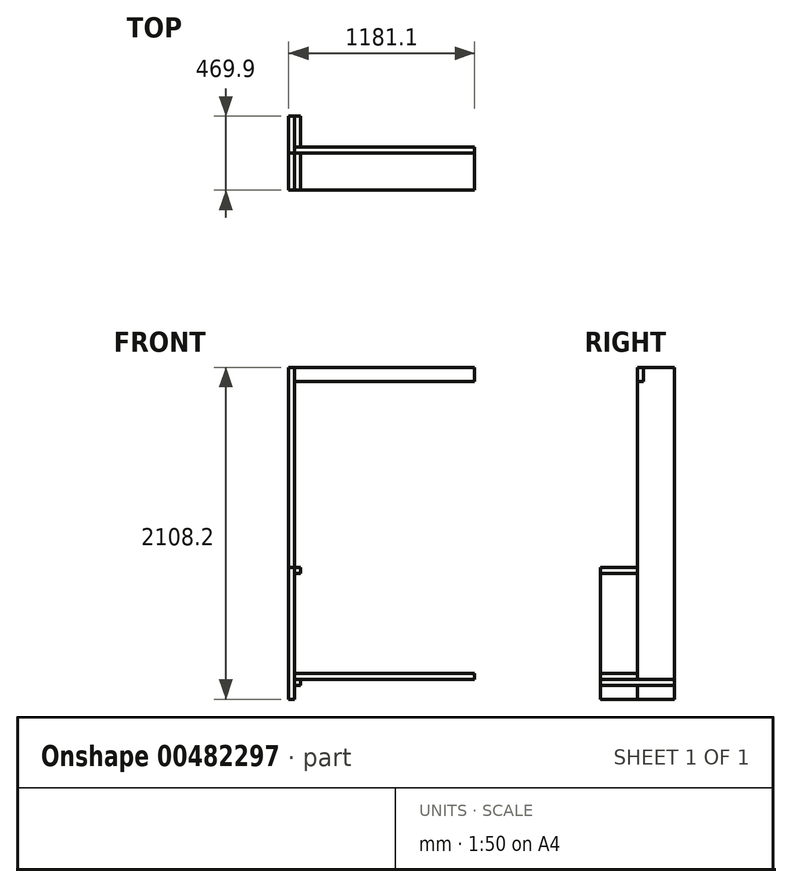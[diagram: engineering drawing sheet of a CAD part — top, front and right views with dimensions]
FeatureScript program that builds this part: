
annotation { "Feature Type Name" : "Feature", "Feature Type Description" : "" }
export const myFeature = defineFeature(function(context is Context, id is Id, definition is map)
    precondition{}
    {
        {
            var Q0;
            Q0=qCreatedBy(makeId("Top.planeOp"),FACE);
            var sketch = newSketch(context, id + "F0", { "sketchPlane" : qUnion([Q0])});
            skLineSegment(sketch, "E0.bottom", {"start": v(0, 0) * mm, "end": v(38.1, 0) * mm});
            skLineSegment(sketch, "E0.top", {"start": v(0, -234.95) * mm, "end": v(38.1, -234.95) * mm});
            skLineSegment(sketch, "E0.left", {"start": v(0, 0) * mm, "end": v(0, -234.95) * mm});
            skLineSegment(sketch, "E0.right", {"start": v(38.1, 0) * mm, "end": v(38.1, -234.95) * mm});
            skSolve(sketch);
        }
        {
            var Q0;
            Q0 = qSketchRegion(id + "F0", true);
            extrude(context, id + "F1", {"entities" : qUnion([Q0]), "depth" : 2108.2 * mm});
        }
        {
            var Q0;
            Q0=qCreatedBy(makeId("Top.planeOp"),FACE);
            var sketch = newSketch(context, id + "F2", { "sketchPlane" : qUnion([Q0])});
            skPoint(sketch, "E1.0", {"position": v(0, -234.95) * mm});
            skLineSegment(sketch, "E2.bottom", {"start": v(0, -234.95) * mm, "end": v(38.1, -234.95) * mm});
            skLineSegment(sketch, "E2.top", {"start": v(0, -469.9) * mm, "end": v(38.1, -469.9) * mm});
            skLineSegment(sketch, "E2.left", {"start": v(0, -234.95) * mm, "end": v(0, -469.9) * mm});
            skLineSegment(sketch, "E2.right", {"start": v(38.1, -234.95) * mm, "end": v(38.1, -469.9) * mm});
            skSolve(sketch);
        }
        {
            var Q0;
            Q0 = qSketchRegion(id + "F2", true);
            extrude(context, id + "F3", {"entities" : qUnion([Q0]), "depth" : 838.2 * mm});
        }
        {
            var Q0;
            Q0=makeQuery(id+"F3.opExtrude","SWEPT_FACE",FACE,{"disambiguationData":[OSD([sQuery(id+"F2.wireOp",EDGE,"E2.right")])]});
            var sketch = newSketch(context, id + "F4", { "sketchPlane" : qUnion([Q0])});
            skLineSegment(sketch, "E3.bottom", {"start": v(-469.9, 127) * mm, "end": v(-234.95, 127) * mm});
            skLineSegment(sketch, "E3.top", {"start": v(-469.9, 165.1) * mm, "end": v(-234.95, 165.1) * mm});
            skLineSegment(sketch, "E3.left", {"start": v(-469.9, 127) * mm, "end": v(-469.9, 165.1) * mm});
            skLineSegment(sketch, "E3.right", {"start": v(-234.95, 127) * mm, "end": v(-234.95, 165.1) * mm});
            skSolve(sketch);
        }
        {
            var Q0;
            Q0=makeQuery(id+"F4.imprint","IMPRINT",FACE,{"disambiguationData":[TD([[makeQuery(id+"F4.imprint","IMPRINT",EDGE,{"derivedFrom":sQuery(id+"F4.wireOp",EDGE,"E3.bottom")}),1.0]])]});
            extrude(context, id + "F5", {"entities" : qUnion([Q0]), "depth" : 1143 * mm});
        }
        {
            var Q0;
            Q0=makeQuery(id+"F1.opExtrude","SWEPT_FACE",FACE,{"disambiguationData":[OSD([sQuery(id+"F0.wireOp",EDGE,"E0.right")])]});
            var sketch = newSketch(context, id + "F6", { "sketchPlane" : qUnion([Q0])});
            skLineSegment(sketch, "E4.bottom", {"start": v(-234.95, 2108.2) * mm, "end": v(-196.85, 2108.2) * mm});
            skLineSegment(sketch, "E4.top", {"start": v(-234.95, 2019.3) * mm, "end": v(-196.85, 2019.3) * mm});
            skLineSegment(sketch, "E4.left", {"start": v(-234.95, 2108.2) * mm, "end": v(-234.95, 2019.3) * mm});
            skLineSegment(sketch, "E4.right", {"start": v(-196.85, 2108.2) * mm, "end": v(-196.85, 2019.3) * mm});
            skSolve(sketch);
        }
        {
            var Q0;
            Q0=makeQuery(id+"F6.imprint","IMPRINT",FACE,{"disambiguationData":[TD([[makeQuery(id+"F6.imprint","IMPRINT",EDGE,{"derivedFrom":sQuery(id+"F6.wireOp",EDGE,"E4.bottom")}),1.0]])]});
            extrude(context, id + "F7", {"entities" : qUnion([Q0]), "depth" : 1143 * mm});
        }
        {
            var Q0;
            Q0=makeQuery(id+"F3.opExtrude","SWEPT_FACE",FACE,{"disambiguationData":[OSD([sQuery(id+"F2.wireOp",EDGE,"E2.top")])]});
            var sketch = newSketch(context, id + "F8", { "sketchPlane" : qUnion([Q0])});
            skLineSegment(sketch, "E5.0", {"start": v(38.1, 838.2) * mm, "end": v(38.1, 0) * mm});
            skLineSegment(sketch, "E6.0", {"start": v(1181.1, 127) * mm, "end": v(38.1, 127) * mm});
            skLineSegment(sketch, "E7.bottom", {"start": v(38.1, 127) * mm, "end": v(76.2, 127) * mm});
            skLineSegment(sketch, "E7.top", {"start": v(38.1, 88.9) * mm, "end": v(76.2, 88.9) * mm});
            skLineSegment(sketch, "E7.left", {"start": v(38.1, 127) * mm, "end": v(38.1, 88.9) * mm});
            skLineSegment(sketch, "E7.right", {"start": v(76.2, 127) * mm, "end": v(76.2, 88.9) * mm});
            skSolve(sketch);
        }
        {
            var Q0;
            Q0 = qSketchRegion(id + "F8", true);
            var Q1;
            Q1=makeQuery(id+"F1.opExtrude","SWEPT_FACE",FACE,{"disambiguationData":[OSD([sQuery(id+"F0.wireOp",EDGE,"E0.bottom")])]});
            extrude(context, id + "F9", {"entities" : qUnion([Q0]), "endBound" : BoundingType.UP_TO_SURFACE, "oppositeDirection" : true, "endBoundEntityFace" : qUnion([Q1]), "depth" : 457.2 * mm});
        }
        {
            var Q0;
            Q0=makeQuery(id+"F3.opExtrude","SWEPT_FACE",FACE,{"disambiguationData":[OSD([sQuery(id+"F2.wireOp",EDGE,"E2.top")])]});
            var sketch = newSketch(context, id + "F10", { "sketchPlane" : qUnion([Q0])});
            skLineSegment(sketch, "E8.bottom", {"start": v(38.1, 838.2) * mm, "end": v(76.2, 838.2) * mm});
            skLineSegment(sketch, "E8.top", {"start": v(38.1, 800.1) * mm, "end": v(76.2, 800.1) * mm});
            skLineSegment(sketch, "E8.left", {"start": v(38.1, 838.2) * mm, "end": v(38.1, 800.1) * mm});
            skLineSegment(sketch, "E8.right", {"start": v(76.2, 838.2) * mm, "end": v(76.2, 800.1) * mm});
            skSolve(sketch);
        }
        {
            var Q0;
            Q0 = qSketchRegion(id + "F10", true);
            extrude(context, id + "F11", {"entities" : qUnion([Q0]), "oppositeDirection" : true, "depth" : 234.95 * mm});
        }
    });
